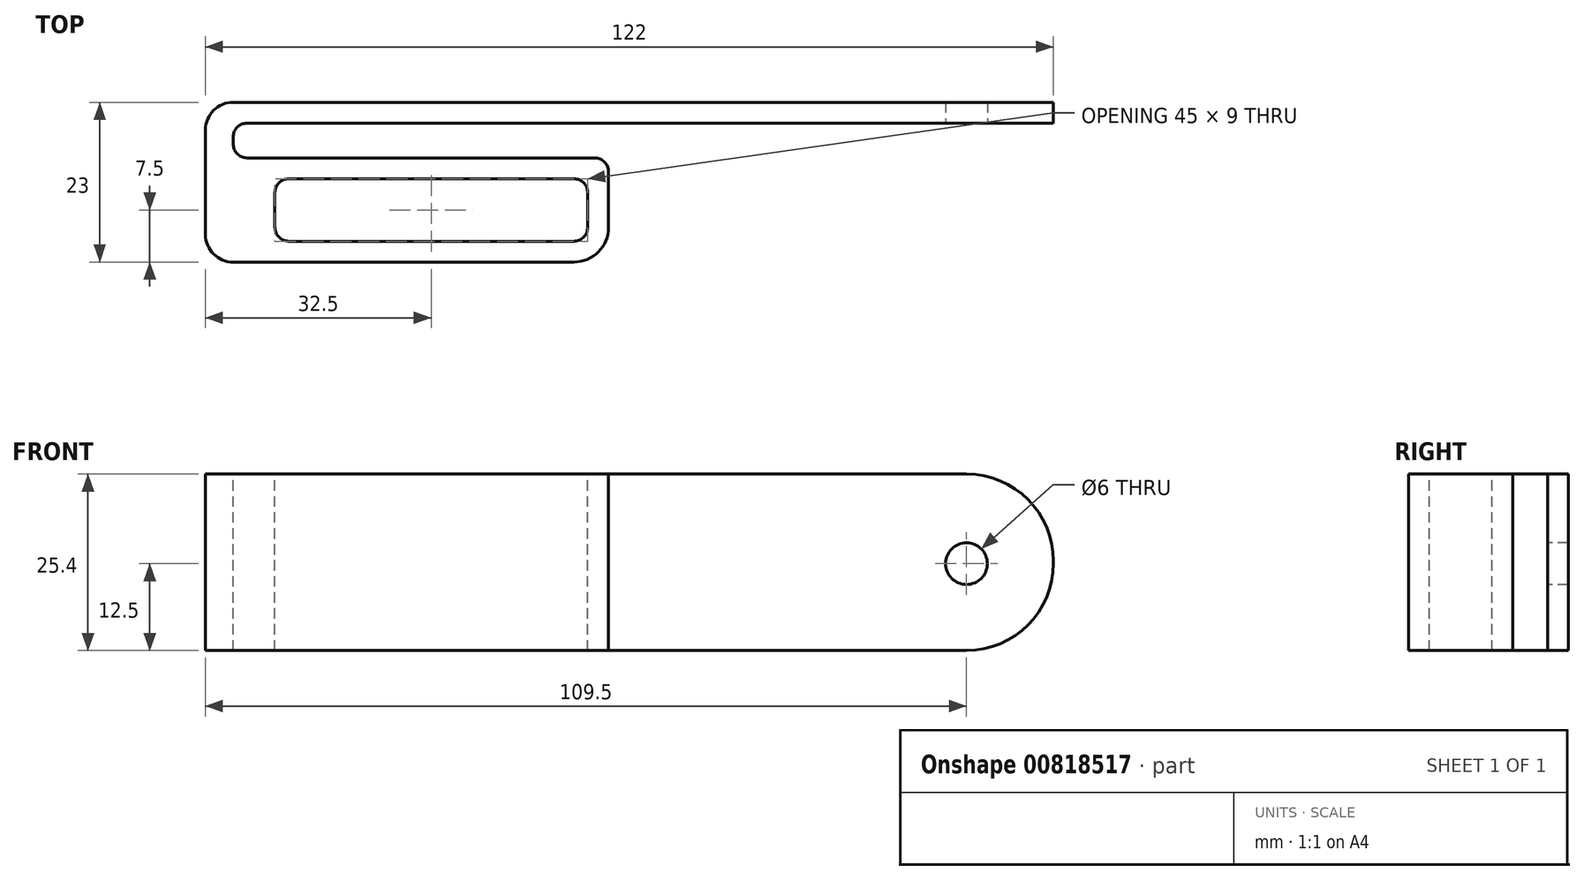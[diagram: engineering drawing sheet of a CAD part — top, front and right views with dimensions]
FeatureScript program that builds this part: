
annotation { "Feature Type Name" : "Feature", "Feature Type Description" : "" }
export const myFeature = defineFeature(function(context is Context, id is Id, definition is map)
    precondition{}
    {
        {
            var Q0;
            Q0=qCreatedBy(makeId("Top.planeOp"),FACE);
            var sketch = newSketch(context, id + "F0", { "sketchPlane" : qUnion([Q0])});
            skLineSegment(sketch, "E0.bottom", {"start": v(0, 0) * mm, "end": v(-118, 0) * mm});
            skLineSegment(sketch, "E0.top", {"start": v(0, -23) * mm, "end": v(-118, -23) * mm});
            skLineSegment(sketch, "E0.left", {"start": v(0, 0) * mm, "end": v(0, -23) * mm});
            skLineSegment(sketch, "E0.right", {"start": v(-122, -4) * mm, "end": v(-122, -19) * mm});
            skPoint(sketch, "E1.visualSharp", {"position": v(-122, 0) * mm});
            skPoint(sketch, "E2.visualSharp", {"position": v(-122, -23) * mm});
            skArc(sketch, "E3.filletArc", {"start": v(-118, 0) * mm, "mid": v(-120.83, -1.17) * mm, "end": v(-122, -4) * mm});
            skArc(sketch, "E4.filletArc", {"start": v(-122, -19) * mm, "mid": v(-120.83, -21.83) * mm, "end": v(-118, -23) * mm});
            skSolve(sketch);
        }
        {
            var Q0;
            Q0 = qSketchRegion(id + "F0", true);
            extrude(context, id + "F1", {"entities" : qUnion([Q0]), "depth" : 25.4 * mm, "offsetDistance" : 25.4 * mm});
        }
        {
            var Q0;
            Q0=makeQuery(id+"F1.opExtrude","CAP_FACE",FACE,{"disambiguationData":[OSD([sQuery(id+"F0.wireOp",EDGE,"E0.bottom"),sQuery(id+"F0.wireOp",EDGE,"E0.top"),sQuery(id+"F0.wireOp",EDGE,"E0.left"),sQuery(id+"F0.wireOp",EDGE,"E0.right")])],"isStart":false});
            var sketch = newSketch(context, id + "F2", { "sketchPlane" : qUnion([Q0])});
            skLineSegment(sketch, "E5.bottom", {"start": v(-110, -11) * mm, "end": v(-69, -11) * mm});
            skLineSegment(sketch, "E5.top", {"start": v(-110, -20) * mm, "end": v(-69, -20) * mm});
            skLineSegment(sketch, "E5.left", {"start": v(-112, -13) * mm, "end": v(-112, -18) * mm});
            skLineSegment(sketch, "E5.right", {"start": v(-67, -13) * mm, "end": v(-67, -18) * mm});
            skPoint(sketch, "E6.visualSharp", {"position": v(-112, -11) * mm});
            skArc(sketch, "E6.filletArc", {"start": v(-110, -11) * mm, "mid": v(-111.41, -11.59) * mm, "end": v(-112, -13) * mm});
            skPoint(sketch, "E7.visualSharp", {"position": v(-112, -20) * mm});
            skArc(sketch, "E7.filletArc", {"start": v(-112, -18) * mm, "mid": v(-111.41, -19.41) * mm, "end": v(-110, -20) * mm});
            skPoint(sketch, "E8.visualSharp", {"position": v(-67, -11) * mm});
            skArc(sketch, "E8.filletArc", {"start": v(-67, -13) * mm, "mid": v(-67.59, -11.59) * mm, "end": v(-69, -11) * mm});
            skPoint(sketch, "E9.visualSharp", {"position": v(-67, -20) * mm});
            skArc(sketch, "E9.filletArc", {"start": v(-69, -20) * mm, "mid": v(-67.59, -19.41) * mm, "end": v(-67, -18) * mm});
            skSolve(sketch);
        }
        {
            var Q0;
            Q0 = qSketchRegion(id + "F2", true);
            extrude(context, id + "F3", {"entities" : qUnion([Q0]), "operationType" : NewBodyOperationType.REMOVE, "endBound" : BoundingType.THROUGH_ALL, "oppositeDirection" : true, "depth" : 25.4 * mm, "offsetDistance" : 25.4 * mm});
        }
        {
            var Q0;
            Q0=makeQuery(id+"F1.opExtrude","CAP_FACE",FACE,{"disambiguationData":[OSD([sQuery(id+"F0.wireOp",EDGE,"E0.bottom"),sQuery(id+"F0.wireOp",EDGE,"E0.top"),sQuery(id+"F0.wireOp",EDGE,"E0.left"),sQuery(id+"F0.wireOp",EDGE,"E0.right"),sQuery(id+"F0.wireOp",EDGE,"E1.filletArc"),sQuery(id+"F0.wireOp",EDGE,"E2.filletArc")])],"isStart":false});
            var sketch = newSketch(context, id + "F4", { "sketchPlane" : qUnion([Q0])});
            skLineSegment(sketch, "E10.0", {"start": v(-64, -8) * mm, "end": v(-64, -18) * mm});
            skArc(sketch, "E10.1", {"start": v(-69, -23) * mm, "mid": v(-65.46, -21.54) * mm, "end": v(-64, -18) * mm});
            skLineSegment(sketch, "E11.0", {"start": v(0, -3) * mm, "end": v(-118, -3) * mm});
            skLineSegment(sketch, "E12.0", {"start": v(0, -3) * mm, "end": v(0, -23) * mm});
            skLineSegment(sketch, "E13.0", {"start": v(0, -23) * mm, "end": v(-69, -23) * mm});
            skPoint(sketch, "E14.orphan", {"position": v(0, -23) * mm});
            skPoint(sketch, "E15.orphan", {"position": v(0, 0) * mm});
            skLineSegment(sketch, "E16.0", {"start": v(-118, -8) * mm, "end": v(-64, -8) * mm});
            skLineSegment(sketch, "E17.0", {"start": v(-118, -3) * mm, "end": v(-118, -8) * mm});
            skSolve(sketch);
        }
        {
            var Q0;
            Q0 = qSketchRegion(id + "F4", true);
            extrude(context, id + "F5", {"entities" : qUnion([Q0]), "operationType" : NewBodyOperationType.REMOVE, "endBound" : BoundingType.THROUGH_ALL, "oppositeDirection" : true, "depth" : 25.4 * mm, "offsetDistance" : 25.4 * mm});
        }
        {
            var Q0;
            Q0=makeQuery(id+"F5.boolean.opBoolean","COPY",EDGE,{"derivedFrom":makeQuery(id+"F5.opExtrude","SWEPT_EDGE",EDGE,{"disambiguationData":[OSD([sQuery(id+"F4.wireOp",EDGE,"E11.0"),sQuery(id+"F4.wireOp",EDGE,"E17.0")])]})});
            var Q1;
            Q1=makeQuery(id+"F5.boolean.opBoolean","COPY",EDGE,{"derivedFrom":makeQuery(id+"F5.opExtrude","SWEPT_EDGE",EDGE,{"disambiguationData":[OSD([sQuery(id+"F4.wireOp",EDGE,"E16.0"),sQuery(id+"F4.wireOp",EDGE,"E17.0")])]})});
            var Q2;
            Q2=makeQuery(id+"F5.boolean.opBoolean","COPY",EDGE,{"derivedFrom":makeQuery(id+"F5.opExtrude","SWEPT_EDGE",EDGE,{"disambiguationData":[OSD([sQuery(id+"F4.wireOp",EDGE,"E10.0"),sQuery(id+"F4.wireOp",EDGE,"E16.0")])]})});
            fillet(context, id + "F6", {"entities" : qUnion([Q0, Q1, Q2]), "radius" : 2 * mm, "tangentPropagation" : true, "allowEdgeOverflow" : false});
        }
        {
            var Q0;
            Q0=makeQuery(id+"F1.opExtrude","CAP_EDGE",EDGE,{"disambiguationData":[OSD([sQuery(id+"F0.wireOp",EDGE,"E0.left")])],"isStart":false});
            var Q1;
            Q1=makeQuery(id+"F1.opExtrude","CAP_EDGE",EDGE,{"disambiguationData":[OSD([sQuery(id+"F0.wireOp",EDGE,"E0.left")])],"isStart":true});
            fillet(context, id + "F7", {"entities" : qUnion([Q0, Q1]), "radius" : 12.5 * mm, "tangentPropagation" : true, "allowEdgeOverflow" : false});
        }
        {
            var Q0;
            Q0=makeQuery(id+"F5.boolean.opBoolean","COPY",FACE,{"derivedFrom":makeQuery(id+"F5.opExtrude","SWEPT_FACE",FACE,{"disambiguationData":[OSD([sQuery(id+"F4.wireOp",EDGE,"E11.0")])]})});
            var sketch = newSketch(context, id + "F8", { "sketchPlane" : qUnion([Q0])});
            skCircle(sketch, "E18", {"center": v(-12.5, 12.5) * mm, "radius": 3 * mm});
            skLineSegment(sketch, "E19", {"start": v(-64, 12.7) * mm, "end": v(-12.5, 12.5) * mm, "construction": true});
            skSolve(sketch);
        }
        {
            var Q0;
            Q0 = qSketchRegion(id + "F8", true);
            extrude(context, id + "F9", {"entities" : qUnion([Q0]), "operationType" : NewBodyOperationType.REMOVE, "endBound" : BoundingType.THROUGH_ALL, "oppositeDirection" : true, "depth" : 25.4 * mm, "offsetDistance" : 25.4 * mm});
        }
    });
